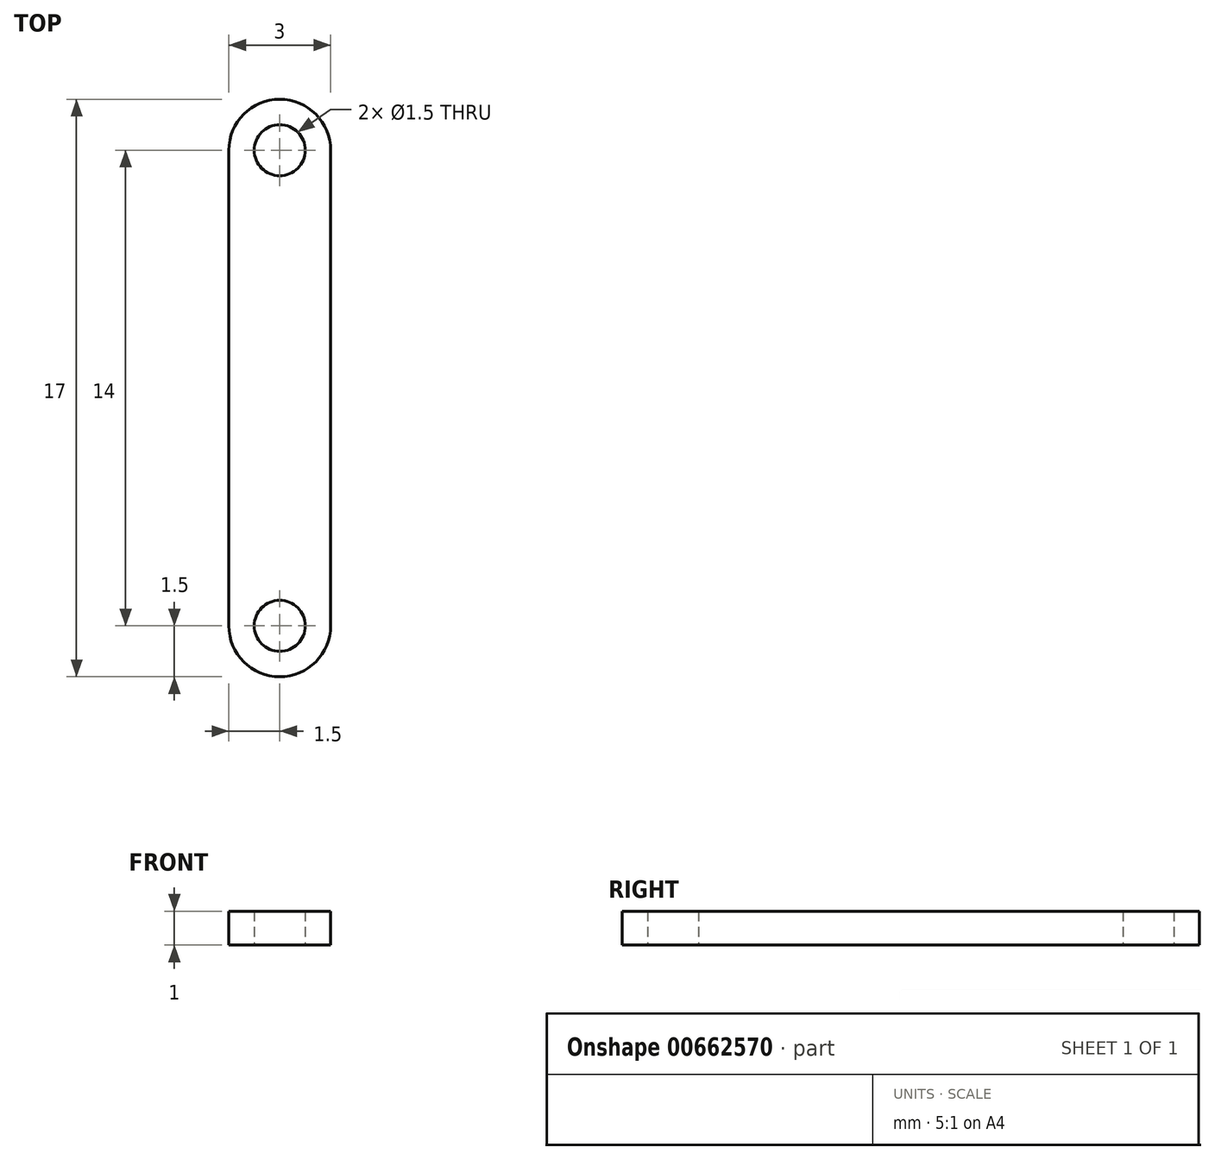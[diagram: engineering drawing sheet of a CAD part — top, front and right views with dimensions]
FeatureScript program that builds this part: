
annotation { "Feature Type Name" : "Feature", "Feature Type Description" : "" }
export const myFeature = defineFeature(function(context is Context, id is Id, definition is map)
    precondition{}
    {
        {
            var Q0;
            Q0=qCreatedBy(makeId("Top.planeOp"),FACE);
            var sketch = newSketch(context, id + "F0", { "sketchPlane" : qUnion([Q0])});
            skLineSegment(sketch, "E0", {"start": v(0, 0) * mm, "end": v(0, 7) * mm});
            skLineSegment(sketch, "E1", {"start": v(3, 7) * mm, "end": v(3, 0) * mm});
            skArc(sketch, "E2", {"start": v(3, 7) * mm, "mid": v(1.5, 8.5) * mm, "end": v(0, 7) * mm});
            skCircle(sketch, "E3", {"center": v(1.5, 7) * mm, "radius": 0.75 * mm});
            skLineSegment(sketch, "E4.MirrorCS", {"start": v(0, 0) * mm, "end": v(0, -7) * mm});
            skLineSegment(sketch, "E5.MirrorCS", {"start": v(3, -7) * mm, "end": v(3, 0) * mm});
            skArc(sketch, "E6.MirrorCS", {"start": v(3, -7) * mm, "mid": v(1.5, -8.5) * mm, "end": v(0, -7) * mm});
            skCircle(sketch, "E7.MirrorC", {"center": v(1.5, -7) * mm, "radius": 0.75 * mm});
            skSolve(sketch);
        }
        {
            var Q0;
            Q0=makeQuery(id+"F0.imprint","IMPRINT",FACE,{"disambiguationData":[TD([[makeQuery(id+"F0.imprint","IMPRINT",EDGE,{"derivedFrom":sQuery(id+"F0.wireOp",EDGE,"E0")}),-1.0]])]});
            extrude(context, id + "F1", {"entities" : qUnion([Q0]), "depth" : 1 * mm, "offsetDistance" : 25 * mm});
        }
    });
